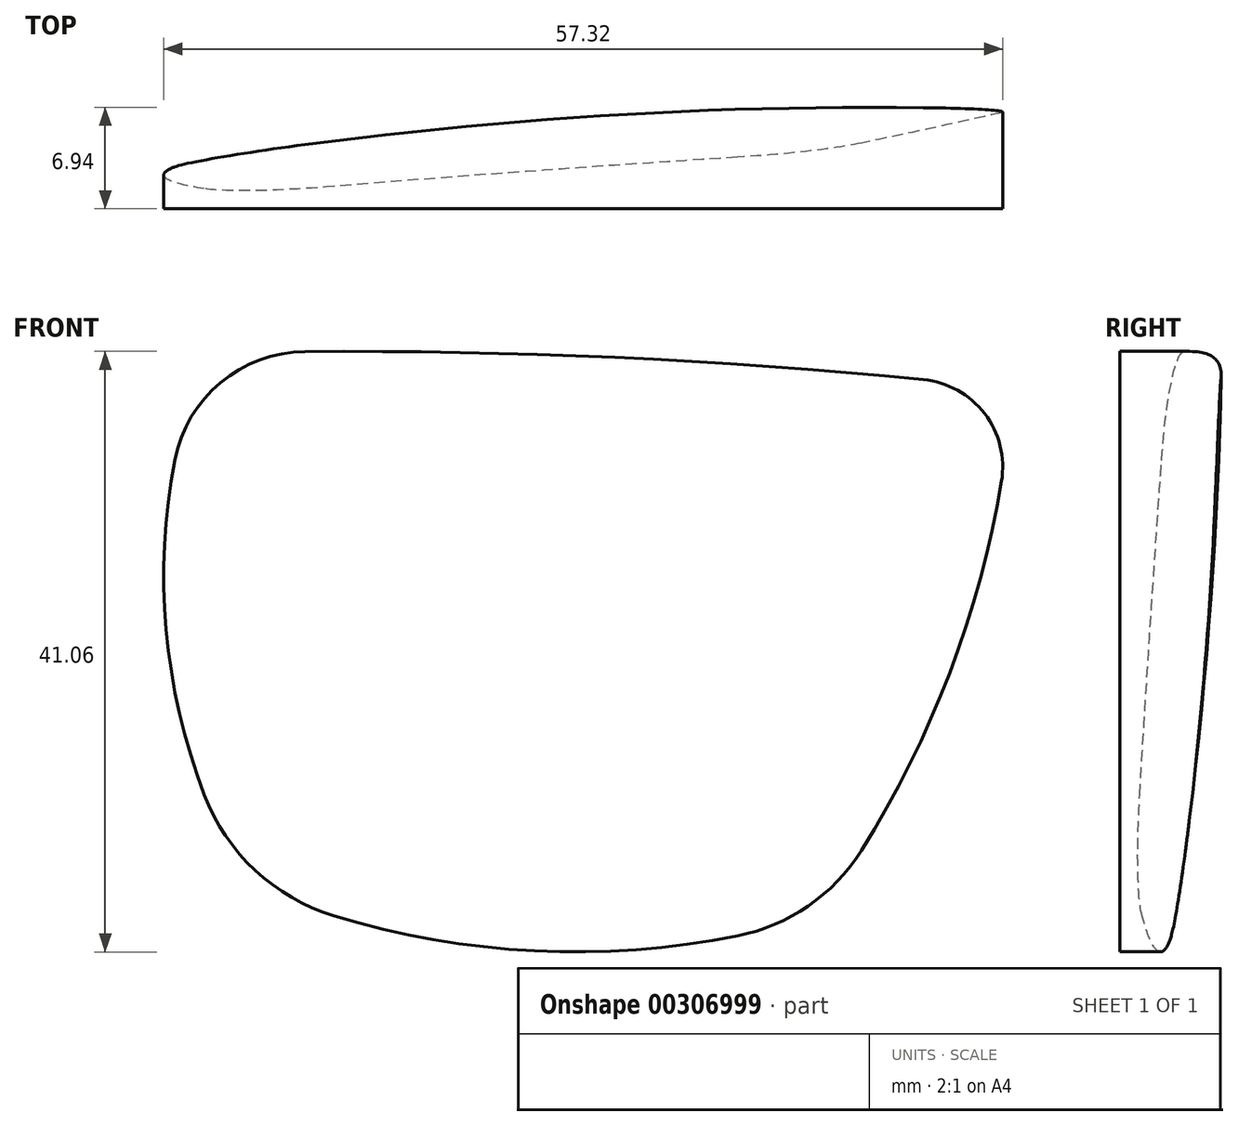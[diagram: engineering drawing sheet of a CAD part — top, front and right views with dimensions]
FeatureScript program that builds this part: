
annotation { "Feature Type Name" : "Feature", "Feature Type Description" : "" }
export const myFeature = defineFeature(function(context is Context, id is Id, definition is map)
    precondition{}
    {
        {
            var Q0;
            Q0=qCreatedBy(makeId("Front.planeOp"),FACE);
            var sketch = newSketch(context, id + "F0", { "sketchPlane" : qUnion([Q0])});
            skArc(sketch, "E0.0.0", {"start": v(-34.1, 10.7) * mm, "mid": v(-34.33, -2) * mm, "end": v(-31.21, -14.33) * mm, "construction": true});
            skArc(sketch, "E0.0.1", {"start": v(-31.21, -14.33) * mm, "mid": v(-26.88, -20.6) * mm, "end": v(-20.26, -24.39) * mm, "construction": true});
            skArc(sketch, "E0.0.2", {"start": v(-20.26, -24.39) * mm, "mid": v(-5.74, -26.92) * mm, "end": v(8.96, -25.84) * mm, "construction": true});
            skArc(sketch, "E0.0.3", {"start": v(8.96, -25.84) * mm, "mid": v(15.05, -23.27) * mm, "end": v(19.63, -18.5) * mm, "construction": true});
            skArc(sketch, "E0.0.4", {"start": v(19.63, -18.5) * mm, "mid": v(26.11, -5.85) * mm, "end": v(30.26, 7.75) * mm, "construction": true});
            skLineSegment(sketch, "E0.0.5", {"start": v(30.26, 7.75) * mm, "end": v(34.76, 7.75) * mm, "construction": true});
            skLineSegment(sketch, "E0.0.6", {"start": v(34.76, 7.75) * mm, "end": v(34.76, 21.75) * mm, "construction": true});
            skLineSegment(sketch, "E0.0.7", {"start": v(34.76, 21.75) * mm, "end": v(-21.24, 21.75) * mm, "construction": true});
            skArc(sketch, "E0.0.8", {"start": v(-21.24, 21.75) * mm, "mid": v(-29.71, 18.6) * mm, "end": v(-34.1, 10.7) * mm, "construction": true});
            skPoint(sketch, "E1.visualSharp", {"position": v(28.45, 17.95) * mm});
            skArc(sketch, "E2", {"start": v(21.01, 15.53) * mm, "mid": v(-0.09, 17.05) * mm, "end": v(-21.24, 17.45) * mm});
            skLineSegment(sketch, "E3", {"start": v(-21.24, 24.56) * mm, "end": v(-21.24, 13.97) * mm, "construction": true});
            skArc(sketch, "E4.filletArc", {"start": v(26.34, 8.57) * mm, "mid": v(25.19, 13.2) * mm, "end": v(21.01, 15.53) * mm});
            skArc(sketch, "E5.0", {"start": v(8.3, -22.5) * mm, "mid": v(13.14, -20.46) * mm, "end": v(16.77, -16.66) * mm});
            skArc(sketch, "E5.2", {"start": v(-28.13, -12.86) * mm, "mid": v(-24.66, -18.02) * mm, "end": v(-19.27, -21.14) * mm});
            skArc(sketch, "E6", {"start": v(16.77, -16.66) * mm, "mid": v(22.8, -4.52) * mm, "end": v(26.34, 8.57) * mm});
            skArc(sketch, "E7", {"start": v(-30.15, 10.02) * mm, "mid": v(-30.74, -1.56) * mm, "end": v(-28.13, -12.86) * mm});
            skArc(sketch, "E8.0", {"start": v(-19.27, -21.14) * mm, "mid": v(-5.57, -23.53) * mm, "end": v(8.3, -22.5) * mm});
            skArc(sketch, "E9", {"start": v(-21.24, 17.45) * mm, "mid": v(-27.03, 15.33) * mm, "end": v(-30.15, 10.02) * mm});
            skSolve(sketch);
        }
        {
            var Q0;
            Q0=makeQuery(id+"F0.imprint","IMPRINT",FACE,{"disambiguationData":[TD([[makeQuery(id+"F0.imprint","IMPRINT",EDGE,{"derivedFrom":sQuery(id+"F0.wireOp",EDGE,"E2")}),1.0]])]});
            extrude(context, id + "F1", {"entities" : qUnion([Q0]), "oppositeDirection" : true, "depth" : 25 * mm});
        }
        {
            var Q0;
            Q0=qCreatedBy(makeId("Top.planeOp"),FACE);
            cPlane(context, id + "F2", {"entities" : qUnion([Q0]), "cplaneType" : CPlaneType.OFFSET, "offset" : 22 * mm, "width" : 150 * mm, "height" : 150 * mm});
        }
        {
            var Q0;
            Q0=qCreatedBy(id+"F2.planeOp",FACE);
            var sketch = newSketch(context, id + "F3", { "sketchPlane" : qUnion([Q0])});
            skArc(sketch, "E10", {"start": v(318, -293) * mm, "mid": v(18, 7) * mm, "end": v(-282, -293) * mm});
            skLineSegment(sketch, "E11", {"start": v(-372.73, -293) * mm, "end": v(417.57, -293) * mm, "construction": true});
            skLineSegment(sketch, "E12", {"start": v(-282, -293) * mm, "end": v(318, -293) * mm});
            skSolve(sketch);
        }
        {
            var Q0;
            Q0=makeQuery(id+"F3.imprint","IMPRINT",FACE,{"disambiguationData":[TD([[makeQuery(id+"F3.imprint","IMPRINT",EDGE,{"derivedFrom":sQuery(id+"F3.wireOp",EDGE,"E10")}),1.0]])]});
            var Q1;
            Q1=sQuery(id+"F3.wireOp",EDGE,"E12");
            revolve(context, id + "F4", {"entities" : qUnion([Q0]), "axis" : qUnion([Q1]), "revolveType" : RevolveType.SYMMETRIC, "angle" : 30 * degree});
        }
        {
            var Q0;
            Q0=makeQuery(id+"F1.opExtrude","SWEPT_BODY",BODY,{"disambiguationData":[OSD([sQuery(id+"F0.wireOp",EDGE,"E2"),sQuery(id+"F0.wireOp",EDGE,"E4.filletArc"),sQuery(id+"F0.wireOp",EDGE,"E5.0"),sQuery(id+"F0.wireOp",EDGE,"E5.2"),sQuery(id+"F0.wireOp",EDGE,"E6"),sQuery(id+"F0.wireOp",EDGE,"E7"),sQuery(id+"F0.wireOp",EDGE,"E8.0"),sQuery(id+"F0.wireOp",EDGE,"E9")])]});
            var Q1;
            Q1=makeQuery(id+"F4.opRevolve","SWEPT_BODY",BODY,{"disambiguationData":[OSD([sQuery(id+"F3.wireOp",EDGE,"E10"),sQuery(id+"F3.wireOp",EDGE,"E12")])]});
            booleanBodies(context, id + "F5", {"operationType" : BooleanOperationType.INTERSECTION, "tools" : qUnion([Q0, Q1])});
        }
    });
